# Revit family: BOWTIE COMBO
name_source: partatom
category: Furniture Systems
units: mm (PartAtom-declared; Revit-internal decimal feet)

## family parameters
Always vertical = Yes
Cut with Voids When Loaded = No
Part Type = Normal
Room Calculation Point = No
Round Connector Dimension = Use Diameter
Shared = No
Work Plane-Based = No

## types (1)
- BOWTIE COMBO
    3" Rectangle Leg = <By Category>
    36" Round Ottoman = F005-36x18
    BASE = Yes
    Base = <By Category>
    Bowtie = F077-28x21x18
    Bowtie 1_Seat Fabric = <By Category>
    Bowtie 1_Side Fabric = <By Category>
    Bowtie 2_Seat Fabric = <By Category>
    Bowtie 2_Side Fabric = <By Category>
    Bowtie 3_Seat Fabric = <By Category>
    Bowtie 3_Side Fabric = <By Category>
    Bowtie 4_Seat Fabric = <By Category>
    Bowtie 4_Side Fabric = <By Category>
    Bowtie 5_Seat Fabric = <By Category>
    Bowtie 5_Side Fabric = <By Category>
    Description = Combo Products - BOWTIE COMBO
    G1 = Yes
    Glide = <By Category>
    Manufacturer = FOMCORE
    Model = BOWTIE COMBO
    Round Ottoman Seat Fabric = <By Category>
    Round Ottoman Side Fabric = <By Category>
    Seat Fabric = <By Category>
    Side Fabric = <By Category>
    URL = https://fomcore.com

## geometry (parser evidence)
native form markers: Sweep x2
no freeform markers — native parametric forms only
